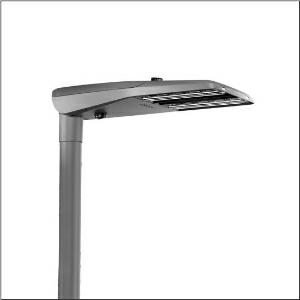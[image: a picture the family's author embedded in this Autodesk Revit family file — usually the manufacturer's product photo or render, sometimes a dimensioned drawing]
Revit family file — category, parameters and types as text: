
# Revit family: streetlight_sl_11_iq_midi___st1_2a_5xc3a51y08le_7352
name_source: partatom
category: Lighting Fixtures
units: mm (PartAtom-declared; Revit-internal decimal feet)

## family parameters
Cut with Voids When Loaded = No
Host = Face
Light Source = No
Part Type = Normal
Room Calculation Point = No
Round Connector Dimension = Use Diameter
Shared = No

## types (1)
- --- (1 x LED, 9210 lm, 59.4 W, 3000K)
    Apparent Load = 59 VA
    CIE Flux Codes = 32 70 96 100 100
    Color Rendering = 70
    Color Temperature = 3000K
    Default Elevation = 1800 mm
    Description = Streetlight SL 11 iQ midi, mast luminaire, primary light control with 3 zone facetted reflector, of plastic, silver coated, highly specular, primary optical cover: cover, of PMMA, transparent, light distribution: ST1.2a, light emission: direct distribution, primary light characteristic: asymmetric, installation type: post-top, side-entry, lamps: LED, High Power LED, rated values: 9.210lm | 59,4W | 155,1lm/W (begin service life); end service life: 9.210lm | 61,6W; at 50% lumin. flux: 4.605lm | 28,5W | 161,6lm/W, colour temperature: 3000K, colour rendering: CRI > 70, light colour: 730, light setting 1 begin service life: 100% | 9.210lm | 59,4W | 155,1lm/W | 3.000K, light setting 1 end service life: 61,6W, further light settings possible, control: pre-setting: logarithmic dimming characteristic, Street-Remote, Auto-Match, Temp-Guard, Lumen-Switch, Night-Set, Smart-Wire, Light-Fading, Desk-Remote (wireless, voltage-free reading and setting of iQ features in the workshop via application-optimized NFC function/RFID function), optimised constant luminous flux control (CLO 2.0), with cable H07RN-F 3x 1.5mm², mains connection: 230..240V, AC, 50/60Hz, connection cable pre-assembled, cable length: 8,5m, luminaire housing, of diecast aluminium, powder-coated, SITECO metallic grey (DB 702S), please order mast flange separately, inclination adjustable without tools: 0°, 5°, 10°, 15° (post-top) | 0°, -5°, -10°, -15° (side-entry), sealing non-destructively replaceable, multi-level sealing system, length: 780mm, width: 376mm, height: 118mm, mast flange for spigot size: 42mm (side-entry): 5XC10008XM4, 60/48mm (side-entry/post-top): 5XC10108XM2, 76/60mm (side-entry/post-top): 5XC10108XM1, equipment: standard, Smart Interface below and above, protection rating (complete): IP66, insulation class (complete): insulation class II (safety insulation), certification: CE, ENEC, ENEC+, VDE, UKCA, impact resistance: IK10, permissible operating ambient temperature for outdoor applications: -25..+50°C, standard-compliant lighting for roads and squares, Environmental Product Declaration (EPD) tested and certified by an independent institute, packaging unit: 1 piece

Light Distribution: ST1.2a
    Height = 118 mm
    Lamp = 1 x LED
    Lamp Light Flux = 9210 lm
    Lamp Power = 59.4 W
    Lamp count = 1
    Length = 780 mm
    Luminous efficacy = 155 lm/W
    Manufacturer = Siteco
    ModVariant = No
    Model = 5XC3A51Y08LE
    Number of Poles = 1
    OnlyDefault = Yes
    Power Factor = 1
    Product Name = Streetlight SL 11 iQ midi | ST1.2a
    Product group = mast luminaire | pylon top
    ProductGroupID = 6100
    Protection Class = Protection class II
    Protection Degree = IP 66
    RLX_Detail_Level = 1
    RLX_Emergency_Light_Flux = 0 lm
    RLX_Emergency_Type = 0
    RLX_Emergency_Type_DB = No
    RlxData = <blob elided: 69829 chars, md5=175adb2b>
    Socket = socket
    Standby Power = 0 W
    System Light Flux = 9210 lm
    System Power = 59 W
    Type Comments = factory setting: luminous flux: 100 % | dim-lin: 254 | 521 mA
    Type Image = l_1004429.jpg
    URL = http://relux.com
    VarID = @adj_132841
    Voltage = 0 V
    Weight = 0.00 kg
    Width = 376 mm

## geometry (parser evidence)
native form markers: Blend x4, Sweep x10
no freeform markers — native parametric forms only
